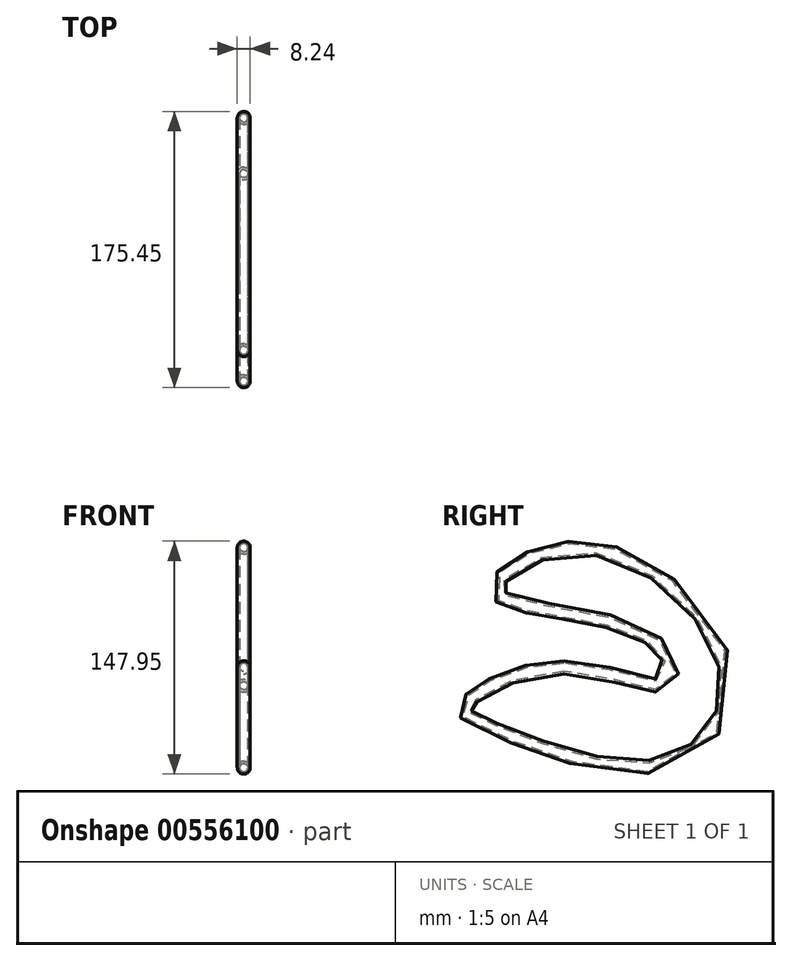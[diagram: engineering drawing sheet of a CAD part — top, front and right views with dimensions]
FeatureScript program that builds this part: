
annotation { "Feature Type Name" : "Feature", "Feature Type Description" : "" }
export const myFeature = defineFeature(function(context is Context, id is Id, definition is map)
    precondition{}
    {
        {
            var Q0;
            Q0=qCreatedBy(makeId("Front.planeOp"),FACE);
            var sketch = newSketch(context, id + "F0", { "sketchPlane" : qUnion([Q0])});
            skCircle(sketch, "E0", {"center": v(0, 0) * mm, "radius": 4.12 * mm});
            skCircle(sketch, "E1", {"center": v(0, 0) * mm, "radius": 2.6 * mm});
            skSolve(sketch);
        }
        {
            var Q0;
            Q0=qCreatedBy(makeId("Right.planeOp"),FACE);
            var sketch = newSketch(context, id + "F1", { "sketchPlane" : qUnion([Q0])});
            skFitSpline(sketch, "E2", {"points": [v(0, 0) * mm, v(-63.03, -25.61) * mm, v(-41.16, -40.58) * mm, v(63.9, -61.6) * mm, v(103.32, -2.6) * mm, v(11.51, 75.98) * mm, v(-42.88, 47.49) * mm, v(52.96, 19.86) * mm, v(65.9, -10.07) * mm, v(0, 0) * mm]});
            skSolve(sketch);
        }
        {
            var Q0;
            Q0 = qSketchRegion(id + "F0", true);
            var Q1;
            Q1 = qConstructionFilter(qBodyType(qCreatedBy(id + "F1" ,EDGE), BodyType.WIRE), ConstructionObject.NO);
            sweep(context, id + "F2", {"profiles" : qUnion([Q0]), "path" : qUnion([Q1])});
        }
    });
